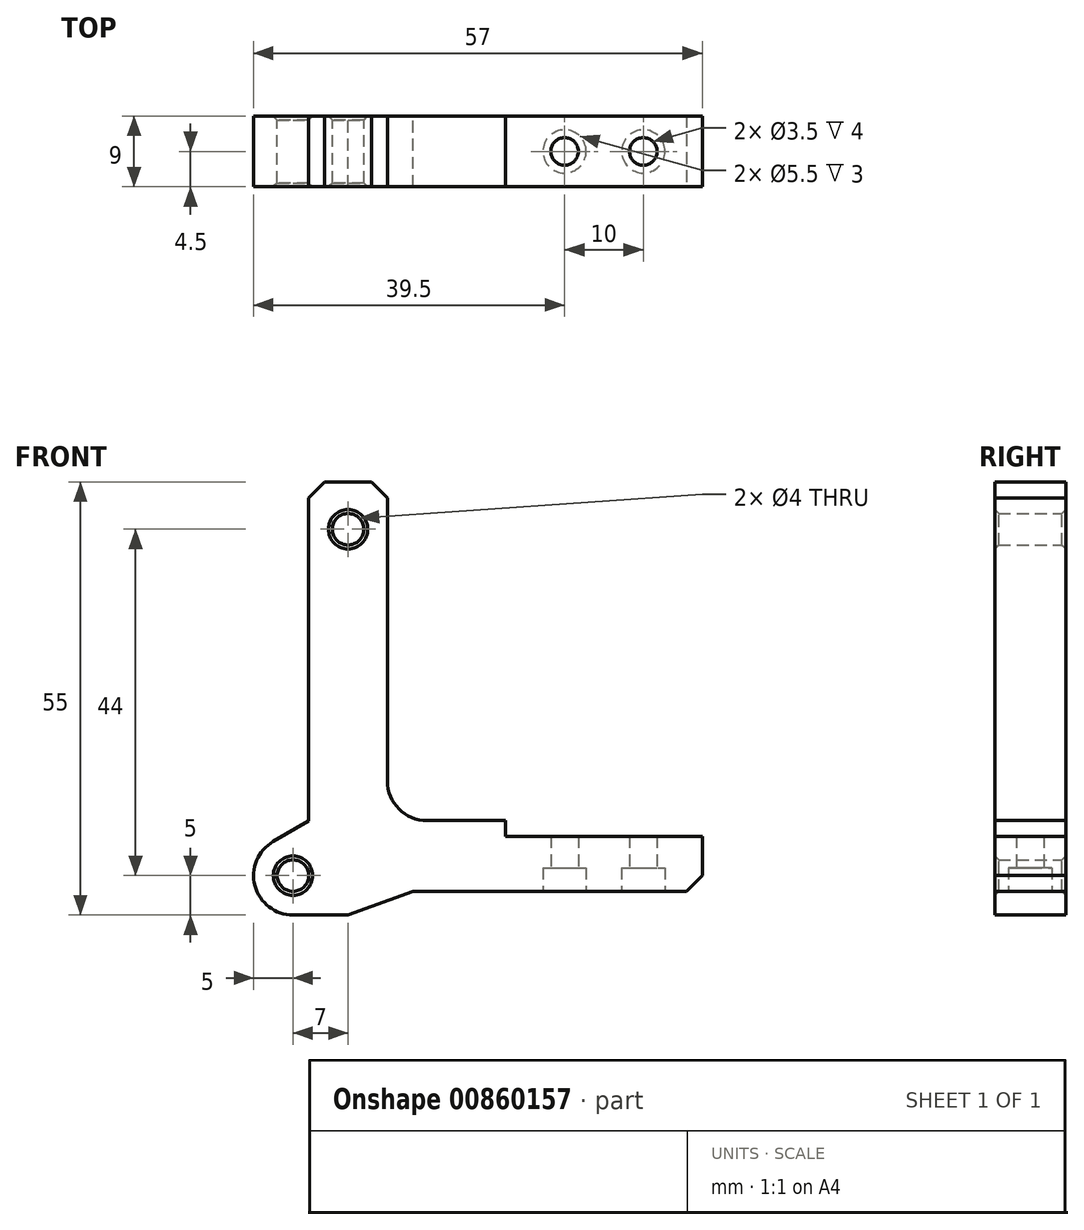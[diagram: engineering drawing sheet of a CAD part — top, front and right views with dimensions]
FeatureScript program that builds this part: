
annotation { "Feature Type Name" : "Feature", "Feature Type Description" : "" }
export const myFeature = defineFeature(function(context is Context, id is Id, definition is map)
    precondition{}
    {
        {
            var Q0;
            Q0=qCreatedBy(makeId("Front.planeOp"),FACE);
            var sketch = newSketch(context, id + "F0", { "sketchPlane" : qUnion([Q0])});
            skArc(sketch, "E0", {"start": v(-2.5, 4.33) * mm, "mid": v(-4.83, -1.3) * mm, "end": v(0, -5) * mm});
            skLineSegment(sketch, "E1", {"start": v(-2.5, 4.33) * mm, "end": v(2, 6.93) * mm});
            skLineSegment(sketch, "E2", {"start": v(2, 6.93) * mm, "end": v(2, 50) * mm});
            skLineSegment(sketch, "E3", {"start": v(2, 50) * mm, "end": v(12, 50) * mm});
            skLineSegment(sketch, "E4", {"start": v(12, 50) * mm, "end": v(12, 7) * mm});
            skLineSegment(sketch, "E5", {"start": v(12, 7) * mm, "end": v(27, 7) * mm});
            skLineSegment(sketch, "E6", {"start": v(27, 7) * mm, "end": v(27, 5) * mm});
            skLineSegment(sketch, "E7", {"start": v(27, 5) * mm, "end": v(52, 5) * mm});
            skLineSegment(sketch, "E8", {"start": v(52, 5) * mm, "end": v(52, -2) * mm});
            skLineSegment(sketch, "E9", {"start": v(52, -2) * mm, "end": v(15.24, -2) * mm});
            skLineSegment(sketch, "E10", {"start": v(15.24, -2) * mm, "end": v(7, -5) * mm});
            skLineSegment(sketch, "E11", {"start": v(7, -5) * mm, "end": v(0, -5) * mm});
            skCircle(sketch, "E12", {"center": v(0, 0) * mm, "radius": 2 * mm});
            skCircle(sketch, "E13", {"center": v(7, 44) * mm, "radius": 2 * mm});
            skSolve(sketch);
        }
        {
            var Q0;
            Q0 = qSketchRegion(id + "F0", true);
            extrude(context, id + "F1", {"entities" : qUnion([Q0]), "endBound" : BoundingType.SYMMETRIC, "depth" : 9 * mm, "offsetDistance" : 25 * mm});
        }
        {
            var Q0;
            Q0=makeQuery(id+"F1.opExtrude","CAP_EDGE",EDGE,{"disambiguationData":[OSD([sQuery(id+"F0.wireOp",EDGE,"E13")])],"isStart":false});
            var Q1;
            Q1=makeQuery(id+"F1.opExtrude","CAP_EDGE",EDGE,{"disambiguationData":[OSD([sQuery(id+"F0.wireOp",EDGE,"E12")])],"isStart":false});
            var Q2;
            Q2=makeQuery(id+"F1.opExtrude","CAP_EDGE",EDGE,{"disambiguationData":[OSD([sQuery(id+"F0.wireOp",EDGE,"E13")])],"isStart":true});
            var Q3;
            Q3=makeQuery(id+"F1.opExtrude","CAP_EDGE",EDGE,{"disambiguationData":[OSD([sQuery(id+"F0.wireOp",EDGE,"E12")])],"isStart":true});
            chamfer(context, id + "F2", {"entities" : qUnion([Q0, Q1, Q2, Q3]), "width" : 0.5 * mm, "tangentPropagation" : true});
        }
        {
            var Q0;
            Q0=makeQuery(id+"F1.opExtrude","SWEPT_EDGE",EDGE,{"disambiguationData":[OSD([sQuery(id+"F0.wireOp",EDGE,"E3"),sQuery(id+"F0.wireOp",EDGE,"E4")])]});
            var Q1;
            Q1=makeQuery(id+"F1.opExtrude","SWEPT_EDGE",EDGE,{"disambiguationData":[OSD([sQuery(id+"F0.wireOp",EDGE,"E2"),sQuery(id+"F0.wireOp",EDGE,"E3")])]});
            var Q2;
            Q2=makeQuery(id+"F1.opExtrude","SWEPT_EDGE",EDGE,{"disambiguationData":[OSD([sQuery(id+"F0.wireOp",EDGE,"E8"),sQuery(id+"F0.wireOp",EDGE,"E9")])]});
            chamfer(context, id + "F3", {"entities" : qUnion([Q0, Q1, Q2]), "width" : 2 * mm, "tangentPropagation" : true});
        }
        {
            var Q0;
            Q0=makeQuery(id+"F1.opExtrude","SWEPT_EDGE",EDGE,{"disambiguationData":[OSD([sQuery(id+"F0.wireOp",EDGE,"E4"),sQuery(id+"F0.wireOp",EDGE,"E5")])]});
            fillet(context, id + "F4", {"entities" : qUnion([Q0]), "radius" : 5 * mm, "tangentPropagation" : true, "allowEdgeOverflow" : false});
        }
        {
            var Q0;
            Q0=makeQuery(id+"F1.opExtrude","SWEPT_FACE",FACE,{"disambiguationData":[OSD([sQuery(id+"F0.wireOp",EDGE,"E9")])]});
            var sketch = newSketch(context, id + "F5", { "sketchPlane" : qUnion([Q0])});
            skPoint(sketch, "E14", {"position": v(44.5, 0) * mm});
            skPoint(sketch, "E15", {"position": v(34.5, 0) * mm});
            skSolve(sketch);
        }
        {
            var Q0;
            Q0=sQuery(id+"F5.wireOp",VERTEX,"E14");
            var Q1;
            Q1=sQuery(id+"F5.wireOp",VERTEX,"E15");
            var Q2;
            Q2=makeQuery(id+"F1.opExtrude","SWEPT_BODY",BODY,{"disambiguationData":[OSD([sQuery(id+"F0.wireOp",EDGE,"E0"),sQuery(id+"F0.wireOp",EDGE,"E1"),sQuery(id+"F0.wireOp",EDGE,"E2"),sQuery(id+"F0.wireOp",EDGE,"E3"),sQuery(id+"F0.wireOp",EDGE,"E4"),sQuery(id+"F0.wireOp",EDGE,"E5"),sQuery(id+"F0.wireOp",EDGE,"E6"),sQuery(id+"F0.wireOp",EDGE,"E7"),sQuery(id+"F0.wireOp",EDGE,"E8"),sQuery(id+"F0.wireOp",EDGE,"E9"),sQuery(id+"F0.wireOp",EDGE,"E10"),sQuery(id+"F0.wireOp",EDGE,"E11"),sQuery(id+"F0.wireOp",EDGE,"E12"),sQuery(id+"F0.wireOp",EDGE,"E13")])]});
            hole(context, id + "F6", {"style" : HoleStyle.C_BORE, "endStyle" : HoleEndStyle.THROUGH, "holeDiameter" : 3.5 * mm, "cBoreDiameter" : 5.5 * mm, "cBoreDepth" : 3 * mm, "majorDiameter" : 3 * mm, "isTappedThrough" : true, "tappedDepth" : 1.5 * mm, "tapClearance" : 3, "startFromSketch" : true, "locations" : qUnion([Q0, Q1]), "scope" : qUnion([Q2])});
        }
    });
